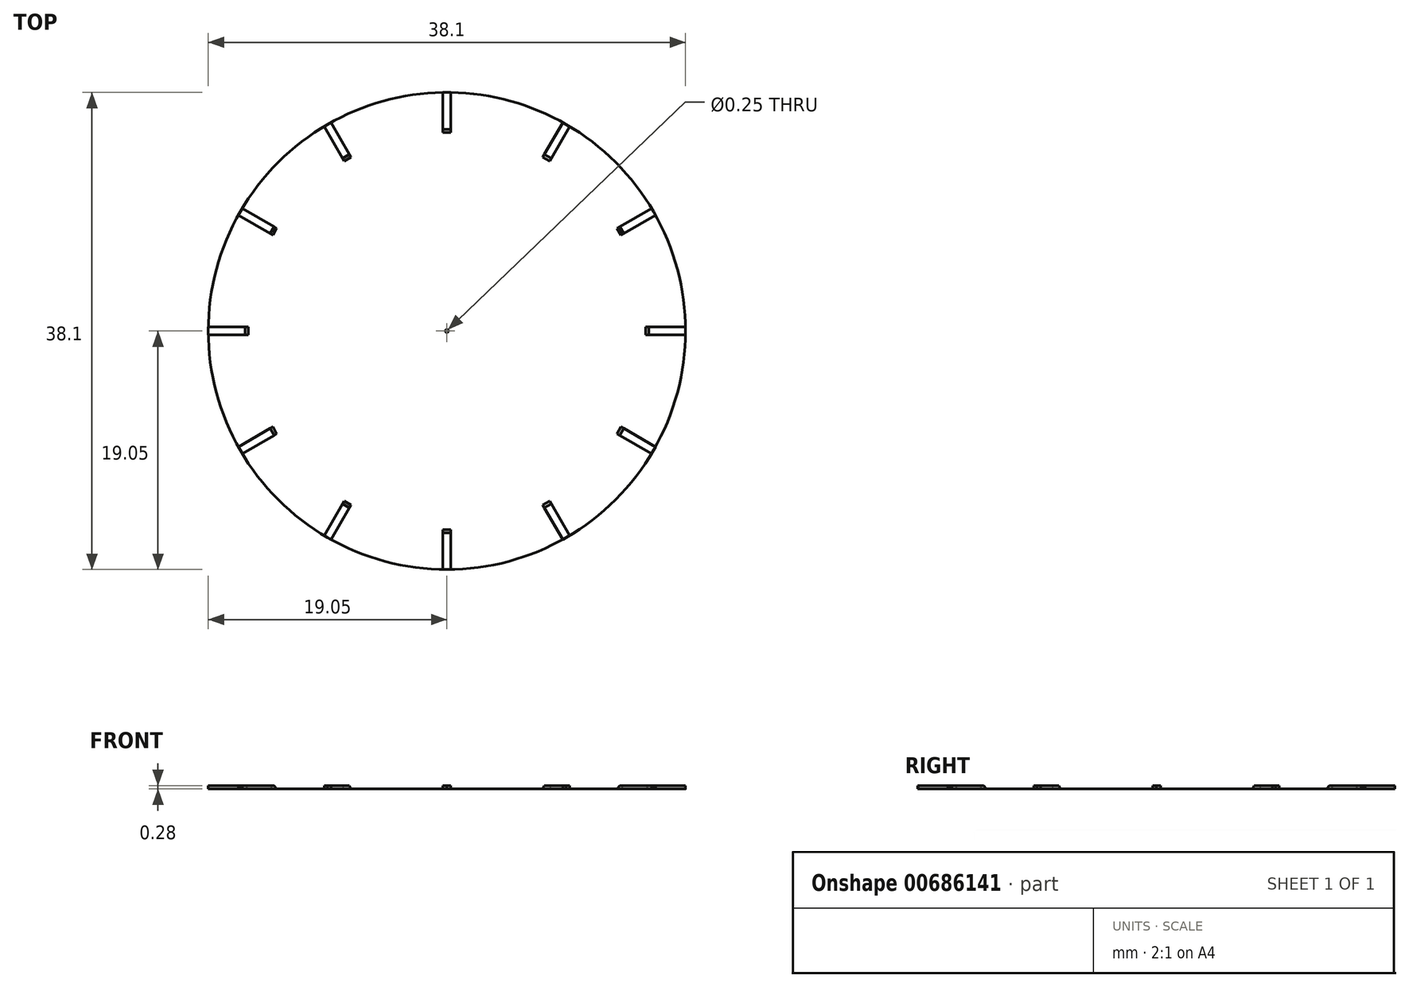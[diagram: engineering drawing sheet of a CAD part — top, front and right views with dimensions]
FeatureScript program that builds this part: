
annotation { "Feature Type Name" : "Feature", "Feature Type Description" : "" }
export const myFeature = defineFeature(function(context is Context, id is Id, definition is map)
    precondition{}
    {
        {
            var Q0;
            Q0=qCreatedBy(makeId("Top.planeOp"),FACE);
            var sketch = newSketch(context, id + "F0", { "sketchPlane" : qUnion([Q0])});
            skCircle(sketch, "E0", {"center": v(0, 0) * mm, "radius": 19.05 * mm});
            skSolve(sketch);
        }
        {
            var Q0;
            Q0=makeQuery(id+"F0.imprint","IMPRINT",FACE,{"disambiguationData":[TD([[makeQuery(id+"F0.imprint","IMPRINT",EDGE,{"derivedFrom":sQuery(id+"F0.wireOp",EDGE,"E0")}),1.0]])]});
            extrude(context, id + "F1", {"entities" : qUnion([Q0]), "depth" : 0.03 * mm, "offsetDistance" : 25.4 * mm});
        }
        {
            var Q0;
            Q0=makeQuery(id+"F1.opExtrude","CAP_FACE",FACE,{"disambiguationData":[OSD([sQuery(id+"F0.wireOp",EDGE,"E0")])],"isStart":false});
            var sketch = newSketch(context, id + "F2", { "sketchPlane" : qUnion([Q0])});
            skCircle(sketch, "E1", {"center": v(0, 0) * mm, "radius": 0.13 * mm});
            skSolve(sketch);
        }
        {
            var Q0;
            Q0=makeQuery(id+"F2.imprint","IMPRINT",FACE,{"disambiguationData":[TD([[makeQuery(id+"F2.imprint","IMPRINT",EDGE,{"derivedFrom":sQuery(id+"F2.wireOp",EDGE,"E1")}),1.0]])]});
            extrude(context, id + "F3", {"entities" : qUnion([Q0]), "operationType" : NewBodyOperationType.REMOVE, "oppositeDirection" : true, "depth" : 25.4 * mm, "offsetDistance" : 25.4 * mm});
        }
        {
            var Q0;
            Q0=makeQuery(id+"F1.opExtrude","CAP_FACE",FACE,{"disambiguationData":[OSD([sQuery(id+"F0.wireOp",EDGE,"E0")])],"isStart":false});
            var sketch = newSketch(context, id + "F4", { "sketchPlane" : qUnion([Q0])});
            skLineSegment(sketch, "E2", {"start": v(0, 0) * mm, "end": v(0, 19.05) * mm});
            skLineSegment(sketch, "E3", {"start": v(0, 19.05) * mm, "end": v(0.32, 19.04) * mm});
            skLineSegment(sketch, "E4", {"start": v(0, 19.05) * mm, "end": v(-0.32, 19.04) * mm});
            skLineSegment(sketch, "E5", {"start": v(-0.32, 15.86) * mm, "end": v(0.32, 15.86) * mm});
            skLineSegment(sketch, "E6", {"start": v(-0.32, 19.05) * mm, "end": v(-0.32, 15.86) * mm});
            skPoint(sketch, "E6.startSnap0", {"position": v(-0.32, 19.04) * mm});
            skLineSegment(sketch, "E7", {"start": v(0.32, 19.04) * mm, "end": v(0.32, 15.86) * mm});
            skPoint(sketch, "E8.orphan", {"position": v(-0.63, 19.04) * mm});
            skPoint(sketch, "E9.orphan", {"position": v(0.63, 15.86) * mm});
            skPoint(sketch, "E10.orphan", {"position": v(0.63, 19.04) * mm});
            skLineSegment(sketch, "E11.1.0", {"start": v(-9.8, 16.34) * mm, "end": v(-8.2, 13.58) * mm});
            skLineSegment(sketch, "E11.1.1", {"start": v(-9.52, 16.5) * mm, "end": v(-9.8, 16.33) * mm});
            skLineSegment(sketch, "E11.1.2", {"start": v(-9.52, 16.5) * mm, "end": v(-9.25, 16.65) * mm});
            skLineSegment(sketch, "E11.1.3", {"start": v(-9.25, 16.65) * mm, "end": v(-7.66, 13.9) * mm});
            skLineSegment(sketch, "E11.1.4", {"start": v(-8.2, 13.58) * mm, "end": v(-7.66, 13.9) * mm});
            skLineSegment(sketch, "E11.2.0", {"start": v(-16.65, 9.25) * mm, "end": v(-13.9, 7.66) * mm});
            skLineSegment(sketch, "E11.2.1", {"start": v(-16.5, 9.52) * mm, "end": v(-16.65, 9.25) * mm});
            skLineSegment(sketch, "E11.2.2", {"start": v(-16.5, 9.52) * mm, "end": v(-16.33, 9.8) * mm});
            skLineSegment(sketch, "E11.2.3", {"start": v(-16.33, 9.8) * mm, "end": v(-13.58, 8.2) * mm});
            skLineSegment(sketch, "E11.2.4", {"start": v(-13.9, 7.66) * mm, "end": v(-13.58, 8.2) * mm});
            skLineSegment(sketch, "E11.3.0", {"start": v(-19.05, -0.32) * mm, "end": v(-15.86, -0.32) * mm});
            skLineSegment(sketch, "E11.3.1", {"start": v(-19.05, 0) * mm, "end": v(-19.04, -0.32) * mm});
            skLineSegment(sketch, "E11.3.2", {"start": v(-19.05, 0) * mm, "end": v(-19.04, 0.32) * mm});
            skLineSegment(sketch, "E11.3.3", {"start": v(-19.04, 0.32) * mm, "end": v(-15.86, 0.32) * mm});
            skLineSegment(sketch, "E11.3.4", {"start": v(-15.86, -0.32) * mm, "end": v(-15.86, 0.32) * mm});
            skLineSegment(sketch, "E11.4.0", {"start": v(-16.34, -9.8) * mm, "end": v(-13.58, -8.2) * mm});
            skLineSegment(sketch, "E11.4.1", {"start": v(-16.5, -9.53) * mm, "end": v(-16.33, -9.8) * mm});
            skLineSegment(sketch, "E11.4.2", {"start": v(-16.5, -9.53) * mm, "end": v(-16.65, -9.25) * mm});
            skLineSegment(sketch, "E11.4.3", {"start": v(-16.65, -9.25) * mm, "end": v(-13.9, -7.66) * mm});
            skLineSegment(sketch, "E11.4.4", {"start": v(-13.58, -8.2) * mm, "end": v(-13.9, -7.66) * mm});
            skLineSegment(sketch, "E11.5.0", {"start": v(-9.25, -16.65) * mm, "end": v(-7.66, -13.9) * mm});
            skLineSegment(sketch, "E11.5.1", {"start": v(-9.52, -16.5) * mm, "end": v(-9.25, -16.65) * mm});
            skLineSegment(sketch, "E11.5.2", {"start": v(-9.52, -16.5) * mm, "end": v(-9.8, -16.33) * mm});
            skLineSegment(sketch, "E11.5.3", {"start": v(-9.8, -16.33) * mm, "end": v(-8.2, -13.58) * mm});
            skLineSegment(sketch, "E11.5.4", {"start": v(-7.66, -13.9) * mm, "end": v(-8.2, -13.58) * mm});
            skLineSegment(sketch, "E11.6.0", {"start": v(0.32, -19.05) * mm, "end": v(0.32, -15.86) * mm});
            skLineSegment(sketch, "E11.6.1", {"start": v(0, -19.05) * mm, "end": v(0.32, -19.04) * mm});
            skLineSegment(sketch, "E11.6.2", {"start": v(0, -19.05) * mm, "end": v(-0.32, -19.04) * mm});
            skLineSegment(sketch, "E11.6.3", {"start": v(-0.32, -19.04) * mm, "end": v(-0.32, -15.86) * mm});
            skLineSegment(sketch, "E11.6.4", {"start": v(0.32, -15.86) * mm, "end": v(-0.32, -15.86) * mm});
            skLineSegment(sketch, "E11.7.0", {"start": v(9.8, -16.34) * mm, "end": v(8.2, -13.58) * mm});
            skLineSegment(sketch, "E11.7.1", {"start": v(9.53, -16.5) * mm, "end": v(9.8, -16.33) * mm});
            skLineSegment(sketch, "E11.7.2", {"start": v(9.53, -16.5) * mm, "end": v(9.25, -16.65) * mm});
            skLineSegment(sketch, "E11.7.3", {"start": v(9.25, -16.65) * mm, "end": v(7.66, -13.9) * mm});
            skLineSegment(sketch, "E11.7.4", {"start": v(8.2, -13.58) * mm, "end": v(7.66, -13.9) * mm});
            skLineSegment(sketch, "E11.8.0", {"start": v(16.65, -9.25) * mm, "end": v(13.9, -7.66) * mm});
            skLineSegment(sketch, "E11.8.1", {"start": v(16.5, -9.52) * mm, "end": v(16.65, -9.25) * mm});
            skLineSegment(sketch, "E11.8.2", {"start": v(16.5, -9.52) * mm, "end": v(16.33, -9.8) * mm});
            skLineSegment(sketch, "E11.8.3", {"start": v(16.33, -9.8) * mm, "end": v(13.58, -8.2) * mm});
            skLineSegment(sketch, "E11.8.4", {"start": v(13.9, -7.66) * mm, "end": v(13.58, -8.2) * mm});
            skLineSegment(sketch, "E11.9.0", {"start": v(19.05, 0.32) * mm, "end": v(15.86, 0.32) * mm});
            skLineSegment(sketch, "E11.9.1", {"start": v(19.05, 0) * mm, "end": v(19.04, 0.32) * mm});
            skLineSegment(sketch, "E11.9.2", {"start": v(19.05, 0) * mm, "end": v(19.04, -0.32) * mm});
            skLineSegment(sketch, "E11.9.3", {"start": v(19.04, -0.32) * mm, "end": v(15.86, -0.32) * mm});
            skLineSegment(sketch, "E11.9.4", {"start": v(15.86, 0.32) * mm, "end": v(15.86, -0.32) * mm});
            skLineSegment(sketch, "E11.10.0", {"start": v(16.34, 9.8) * mm, "end": v(13.58, 8.2) * mm});
            skLineSegment(sketch, "E11.10.1", {"start": v(16.5, 9.53) * mm, "end": v(16.33, 9.8) * mm});
            skLineSegment(sketch, "E11.10.2", {"start": v(16.5, 9.53) * mm, "end": v(16.65, 9.25) * mm});
            skLineSegment(sketch, "E11.10.3", {"start": v(16.65, 9.25) * mm, "end": v(13.9, 7.66) * mm});
            skLineSegment(sketch, "E11.10.4", {"start": v(13.58, 8.2) * mm, "end": v(13.9, 7.66) * mm});
            skLineSegment(sketch, "E11.11.0", {"start": v(9.25, 16.65) * mm, "end": v(7.66, 13.9) * mm});
            skLineSegment(sketch, "E11.11.1", {"start": v(9.53, 16.5) * mm, "end": v(9.25, 16.65) * mm});
            skLineSegment(sketch, "E11.11.2", {"start": v(9.53, 16.5) * mm, "end": v(9.8, 16.33) * mm});
            skLineSegment(sketch, "E11.11.3", {"start": v(9.8, 16.33) * mm, "end": v(8.2, 13.58) * mm});
            skLineSegment(sketch, "E11.11.4", {"start": v(7.66, 13.9) * mm, "end": v(8.2, 13.58) * mm});
            skPoint(sketch, "E11.center", {"position": v(0, 0) * mm});
            skSolve(sketch);
        }
        {
            var Q0;
            {var subQ0=sQuery(id+"F4.wireOp",EDGE,"E3");Q0=makeQuery(id+"F4.imprint","IMPRINT",FACE,{"disambiguationData":[TD([[makeQuery(id+"F4.imprint","IMPRINT",EDGE,{"derivedFrom":subQ0}),-1.0]])]});}
            var Q1;
            {var subQ0=sQuery(id+"F4.wireOp",EDGE,"E4");Q1=makeQuery(id+"F4.imprint","IMPRINT",FACE,{"disambiguationData":[TD([[makeQuery(id+"F4.imprint","IMPRINT",EDGE,{"derivedFrom":subQ0}),1.0]])]});}
            var Q2;
            {var subQ0=sQuery(id+"F4.wireOp",EDGE,"E11.11.1");Q2=makeQuery(id+"F4.imprint","IMPRINT",FACE,{"disambiguationData":[TD([[makeQuery(id+"F4.imprint","IMPRINT",EDGE,{"derivedFrom":subQ0}),1.0]])]});}
            var Q3;
            {var subQ0=sQuery(id+"F4.wireOp",EDGE,"E11.10.1");Q3=makeQuery(id+"F4.imprint","IMPRINT",FACE,{"disambiguationData":[TD([[makeQuery(id+"F4.imprint","IMPRINT",EDGE,{"derivedFrom":subQ0}),1.0]])]});}
            var Q4;
            {var subQ0=sQuery(id+"F4.wireOp",EDGE,"E11.9.1");Q4=makeQuery(id+"F4.imprint","IMPRINT",FACE,{"disambiguationData":[TD([[makeQuery(id+"F4.imprint","IMPRINT",EDGE,{"derivedFrom":subQ0}),1.0]])]});}
            var Q5;
            {var subQ0=sQuery(id+"F4.wireOp",EDGE,"E11.8.1");Q5=makeQuery(id+"F4.imprint","IMPRINT",FACE,{"disambiguationData":[TD([[makeQuery(id+"F4.imprint","IMPRINT",EDGE,{"derivedFrom":subQ0}),1.0]])]});}
            var Q6;
            {var subQ0=sQuery(id+"F4.wireOp",EDGE,"E11.7.1");Q6=makeQuery(id+"F4.imprint","IMPRINT",FACE,{"disambiguationData":[TD([[makeQuery(id+"F4.imprint","IMPRINT",EDGE,{"derivedFrom":subQ0}),1.0]])]});}
            var Q7;
            {var subQ0=sQuery(id+"F4.wireOp",EDGE,"E11.6.1");Q7=makeQuery(id+"F4.imprint","IMPRINT",FACE,{"disambiguationData":[TD([[makeQuery(id+"F4.imprint","IMPRINT",EDGE,{"derivedFrom":subQ0}),1.0]])]});}
            var Q8;
            {var subQ0=sQuery(id+"F4.wireOp",EDGE,"E11.5.1");Q8=makeQuery(id+"F4.imprint","IMPRINT",FACE,{"disambiguationData":[TD([[makeQuery(id+"F4.imprint","IMPRINT",EDGE,{"derivedFrom":subQ0}),1.0]])]});}
            var Q9;
            {var subQ0=sQuery(id+"F4.wireOp",EDGE,"E11.4.1");Q9=makeQuery(id+"F4.imprint","IMPRINT",FACE,{"disambiguationData":[TD([[makeQuery(id+"F4.imprint","IMPRINT",EDGE,{"derivedFrom":subQ0}),1.0]])]});}
            var Q10;
            {var subQ0=sQuery(id+"F4.wireOp",EDGE,"E11.3.1");Q10=makeQuery(id+"F4.imprint","IMPRINT",FACE,{"disambiguationData":[TD([[makeQuery(id+"F4.imprint","IMPRINT",EDGE,{"derivedFrom":subQ0}),1.0]])]});}
            var Q11;
            {var subQ0=sQuery(id+"F4.wireOp",EDGE,"E11.2.1");Q11=makeQuery(id+"F4.imprint","IMPRINT",FACE,{"disambiguationData":[TD([[makeQuery(id+"F4.imprint","IMPRINT",EDGE,{"derivedFrom":subQ0}),1.0]])]});}
            var Q12;
            {var subQ0=sQuery(id+"F4.wireOp",EDGE,"E11.1.1");Q12=makeQuery(id+"F4.imprint","IMPRINT",FACE,{"disambiguationData":[TD([[makeQuery(id+"F4.imprint","IMPRINT",EDGE,{"derivedFrom":subQ0}),1.0]])]});}
            extrude(context, id + "F5", {"entities" : qUnion([Q0, Q1, Q2, Q3, Q4, Q5, Q6, Q7, Q8, Q9, Q10, Q11, Q12]), "operationType" : NewBodyOperationType.ADD, "depth" : 0.25 * mm, "offsetDistance" : 25.4 * mm});
        }
        {
            var Q0;
            Q0=makeQuery(id+"F5.opExtrude","CAP_EDGE",EDGE,{"disambiguationData":[OSD([sQuery(id+"F4.wireOp",EDGE,"E5")])],"isStart":false});
            var Q1;
            Q1=makeQuery(id+"F5.opExtrude","CAP_EDGE",EDGE,{"disambiguationData":[OSD([sQuery(id+"F4.wireOp",EDGE,"E11.11.4")])],"isStart":false});
            var Q2;
            Q2=makeQuery(id+"F5.opExtrude","CAP_EDGE",EDGE,{"disambiguationData":[OSD([sQuery(id+"F4.wireOp",EDGE,"E11.10.4")])],"isStart":false});
            var Q3;
            Q3=makeQuery(id+"F5.opExtrude","CAP_EDGE",EDGE,{"disambiguationData":[OSD([sQuery(id+"F4.wireOp",EDGE,"E11.9.4")])],"isStart":false});
            var Q4;
            Q4=makeQuery(id+"F5.opExtrude","CAP_EDGE",EDGE,{"disambiguationData":[OSD([sQuery(id+"F4.wireOp",EDGE,"E11.8.4")])],"isStart":false});
            var Q5;
            Q5=makeQuery(id+"F5.opExtrude","CAP_EDGE",EDGE,{"disambiguationData":[OSD([sQuery(id+"F4.wireOp",EDGE,"E11.7.4")])],"isStart":false});
            var Q6;
            Q6=makeQuery(id+"F5.opExtrude","CAP_EDGE",EDGE,{"disambiguationData":[OSD([sQuery(id+"F4.wireOp",EDGE,"E11.6.4")])],"isStart":false});
            var Q7;
            Q7=makeQuery(id+"F5.opExtrude","CAP_EDGE",EDGE,{"disambiguationData":[OSD([sQuery(id+"F4.wireOp",EDGE,"E11.5.4")])],"isStart":false});
            var Q8;
            Q8=makeQuery(id+"F5.opExtrude","CAP_EDGE",EDGE,{"disambiguationData":[OSD([sQuery(id+"F4.wireOp",EDGE,"E11.4.4")])],"isStart":false});
            var Q9;
            Q9=makeQuery(id+"F5.opExtrude","CAP_EDGE",EDGE,{"disambiguationData":[OSD([sQuery(id+"F4.wireOp",EDGE,"E11.3.4")])],"isStart":false});
            var Q10;
            Q10=makeQuery(id+"F5.opExtrude","CAP_EDGE",EDGE,{"disambiguationData":[OSD([sQuery(id+"F4.wireOp",EDGE,"E11.2.4")])],"isStart":false});
            var Q11;
            Q11=makeQuery(id+"F5.opExtrude","CAP_EDGE",EDGE,{"disambiguationData":[OSD([sQuery(id+"F4.wireOp",EDGE,"E11.1.4")])],"isStart":false});
            chamfer(context, id + "F6", {"entities" : qUnion([Q0, Q1, Q2, Q3, Q4, Q5, Q6, Q7, Q8, Q9, Q10, Q11]), "width" : 0.25 * mm, "tangentPropagation" : true});
        }
    });
